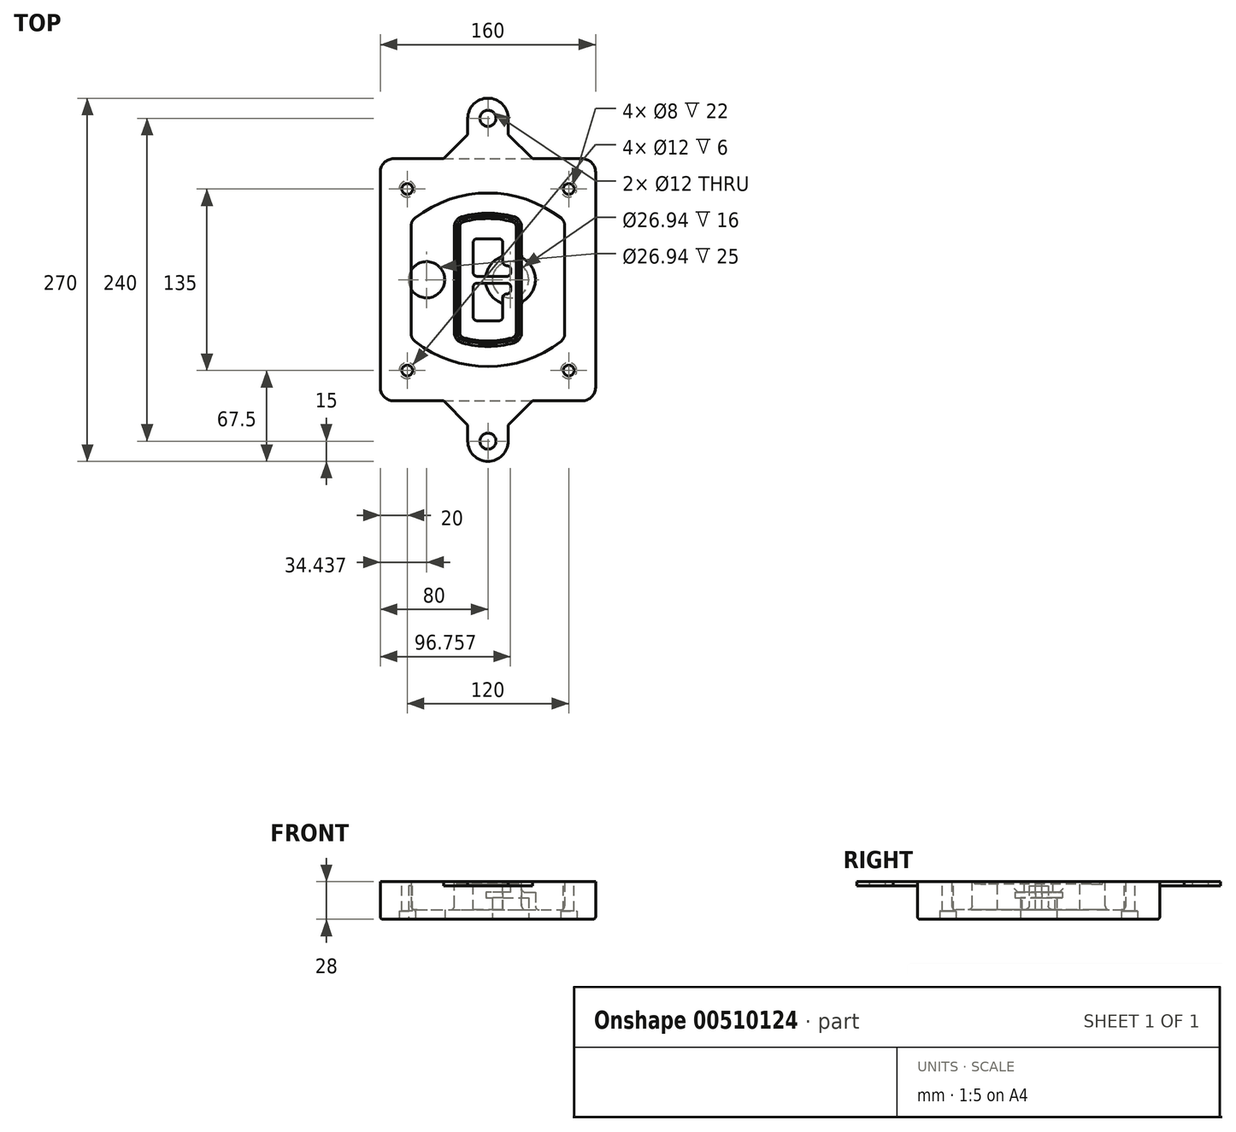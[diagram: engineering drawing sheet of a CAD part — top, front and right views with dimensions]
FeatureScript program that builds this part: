
annotation { "Feature Type Name" : "Feature", "Feature Type Description" : "" }
export const myFeature = defineFeature(function(context is Context, id is Id, definition is map)
    precondition{}
    {
        {
            var Q0;
            Q0=qCreatedBy(makeId("Top.planeOp"),FACE);
            var sketch = newSketch(context, id + "F0", { "sketchPlane" : qUnion([Q0])});
            skPoint(sketch, "E0.rect.middle", {"position": v(0, 0) * mm});
            skLineSegment(sketch, "E1.bottom", {"start": v(-70, -90) * mm, "end": v(70, -90) * mm});
            skLineSegment(sketch, "E1.top", {"start": v(-70, 90) * mm, "end": v(70, 90) * mm});
            skLineSegment(sketch, "E1.left", {"start": v(-80, -80) * mm, "end": v(-80, 80) * mm});
            skLineSegment(sketch, "E1.right", {"start": v(80, -80) * mm, "end": v(80, 80) * mm});
            skLineSegment(sketch, "E2", {"start": v(-80, 90) * mm, "end": v(80, -90) * mm, "construction": true});
            skLineSegment(sketch, "E3", {"start": v(80, 90) * mm, "end": v(-80, -90) * mm, "construction": true});
            skCircle(sketch, "E4", {"center": v(-60, 67.5) * mm, "radius": 4 * mm});
            skCircle(sketch, "E5", {"center": v(60, 67.5) * mm, "radius": 4 * mm});
            skCircle(sketch, "E6", {"center": v(60, -67.5) * mm, "radius": 4 * mm});
            skCircle(sketch, "E7", {"center": v(-60, -67.5) * mm, "radius": 4 * mm});
            skLineSegment(sketch, "E8", {"start": v(-60, 67.5) * mm, "end": v(60, 67.5) * mm, "construction": true});
            skLineSegment(sketch, "E9", {"start": v(60, 67.5) * mm, "end": v(60, -67.5) * mm, "construction": true});
            skLineSegment(sketch, "E10", {"start": v(60, -67.5) * mm, "end": v(-60, -67.5) * mm, "construction": true});
            skLineSegment(sketch, "E11", {"start": v(-60, -67.5) * mm, "end": v(-60, 67.5) * mm, "construction": true});
            skLineSegment(sketch, "E12", {"start": v(-60, 40.3) * mm, "end": v(-60, -40.3) * mm});
            skLineSegment(sketch, "E13", {"start": v(60, 40.3) * mm, "end": v(60, -40.3) * mm});
            skArc(sketch, "E14", {"start": v(56.15, 48.18) * mm, "mid": v(0, 67.5) * mm, "end": v(-56.15, 48.18) * mm});
            skArc(sketch, "E15", {"start": v(-56.15, -48.18) * mm, "mid": v(0, -67.5) * mm, "end": v(56.15, -48.18) * mm});
            skLineSegment(sketch, "E16", {"start": v(-60, 0) * mm, "end": v(60, 0) * mm, "construction": true});
            skPoint(sketch, "E17.visualSharp", {"position": v(-60, -45) * mm});
            skArc(sketch, "E17.filletArc", {"start": v(-60, -40.3) * mm, "mid": v(-58.99, -44.68) * mm, "end": v(-56.15, -48.18) * mm});
            skPoint(sketch, "E18.visualSharp", {"position": v(-60, 45) * mm});
            skArc(sketch, "E18.filletArc", {"start": v(-56.15, 48.18) * mm, "mid": v(-58.99, 44.68) * mm, "end": v(-60, 40.3) * mm});
            skPoint(sketch, "E19.visualSharp", {"position": v(60, 45) * mm});
            skArc(sketch, "E19.filletArc", {"start": v(60, 40.3) * mm, "mid": v(58.99, 44.68) * mm, "end": v(56.15, 48.18) * mm});
            skPoint(sketch, "E20.visualSharp", {"position": v(60, -45) * mm});
            skArc(sketch, "E20.filletArc", {"start": v(56.15, -48.18) * mm, "mid": v(58.99, -44.68) * mm, "end": v(60, -40.3) * mm});
            skPoint(sketch, "E21.visualSharp", {"position": v(-80, 90) * mm});
            skArc(sketch, "E21.filletArc", {"start": v(-70, 90) * mm, "mid": v(-77.07, 87.07) * mm, "end": v(-80, 80) * mm});
            skPoint(sketch, "E22.visualSharp", {"position": v(80, 90) * mm});
            skArc(sketch, "E22.filletArc", {"start": v(80, 80) * mm, "mid": v(77.07, 87.07) * mm, "end": v(70, 90) * mm});
            skPoint(sketch, "E23.visualSharp", {"position": v(80, -90) * mm});
            skArc(sketch, "E23.filletArc", {"start": v(70, -90) * mm, "mid": v(77.07, -87.07) * mm, "end": v(80, -80) * mm});
            skPoint(sketch, "E24.visualSharp", {"position": v(-80, -90) * mm});
            skArc(sketch, "E24.filletArc", {"start": v(-80, -80) * mm, "mid": v(-77.07, -87.07) * mm, "end": v(-70, -90) * mm});
            skArc(sketch, "E25.0", {"start": v(57, 40.3) * mm, "mid": v(56.3, 43.36) * mm, "end": v(54.3, 45.81) * mm});
            skLineSegment(sketch, "E25.1", {"start": v(57, 40.3) * mm, "end": v(57, -40.3) * mm});
            skArc(sketch, "E25.2", {"start": v(54.3, -45.81) * mm, "mid": v(56.3, -43.36) * mm, "end": v(57, -40.3) * mm});
            skArc(sketch, "E25.3", {"start": v(-54.3, -45.81) * mm, "mid": v(0, -64.5) * mm, "end": v(54.3, -45.81) * mm});
            skArc(sketch, "E25.4", {"start": v(-57, -40.3) * mm, "mid": v(-56.3, -43.36) * mm, "end": v(-54.3, -45.81) * mm});
            skArc(sketch, "E25.5", {"start": v(54.3, 45.81) * mm, "mid": v(0, 64.5) * mm, "end": v(-54.3, 45.81) * mm});
            skLineSegment(sketch, "E25.6", {"start": v(-57, 40.3) * mm, "end": v(-57, -40.3) * mm});
            skArc(sketch, "E25.7", {"start": v(-54.3, 45.81) * mm, "mid": v(-56.3, 43.36) * mm, "end": v(-57, 40.3) * mm});
            skArc(sketch, "E26.0", {"start": v(-58.62, 51.33) * mm, "mid": v(-62.58, 46.43) * mm, "end": v(-64, 40.3) * mm});
            skArc(sketch, "E26.1", {"start": v(58.62, 51.33) * mm, "mid": v(0, 71.5) * mm, "end": v(-58.62, 51.33) * mm});
            skArc(sketch, "E26.2", {"start": v(64, 40.3) * mm, "mid": v(62.58, 46.43) * mm, "end": v(58.62, 51.33) * mm});
            skLineSegment(sketch, "E26.3", {"start": v(64, 40.3) * mm, "end": v(64, -40.3) * mm});
            skArc(sketch, "E26.4", {"start": v(58.62, -51.33) * mm, "mid": v(62.58, -46.43) * mm, "end": v(64, -40.3) * mm});
            skLineSegment(sketch, "E26.5", {"start": v(-64, 40.3) * mm, "end": v(-64, -40.3) * mm});
            skArc(sketch, "E26.6", {"start": v(-58.62, -51.33) * mm, "mid": v(0, -71.5) * mm, "end": v(58.62, -51.33) * mm});
            skArc(sketch, "E26.7", {"start": v(-64, -40.3) * mm, "mid": v(-62.58, -46.43) * mm, "end": v(-58.62, -51.33) * mm});
            skSolve(sketch);
        }
        {
            var Q0;
            Q0=makeQuery(id+"F0.imprint","IMPRINT",FACE,{"disambiguationData":[TD([[makeQuery(id+"F0.imprint","IMPRINT",EDGE,{"derivedFrom":sQuery(id+"F0.wireOp",EDGE,"E1.bottom")}),1.0]])]});
            var Q1;
            Q1=makeQuery(id+"F0.imprint","IMPRINT",FACE,{"disambiguationData":[TD([[makeQuery(id+"F0.imprint","IMPRINT",EDGE,{"derivedFrom":sQuery(id+"F0.wireOp",EDGE,"E12")}),1.0]])]});
            var Q2;
            Q2=makeQuery(id+"F0.imprint","IMPRINT",FACE,{"disambiguationData":[TD([[makeQuery(id+"F0.imprint","IMPRINT",EDGE,{"derivedFrom":sQuery(id+"F0.wireOp",EDGE,"E25.0")}),1.0]])]});
            var Q3;
            Q3=makeQuery(id+"F0.imprint","IMPRINT",FACE,{"disambiguationData":[TD([[makeQuery(id+"F0.imprint","IMPRINT",EDGE,{"derivedFrom":sQuery(id+"F0.wireOp",EDGE,"E12")}),-1.0]])]});
            extrude(context, id + "F1", {"entities" : qUnion([Q0, Q1, Q2, Q3]), "oppositeDirection" : true, "depth" : 25 * mm});
        }
        {
            var Q0;
            Q0=makeQuery(id+"F0.imprint","IMPRINT",FACE,{"disambiguationData":[TD([[makeQuery(id+"F0.imprint","IMPRINT",EDGE,{"derivedFrom":sQuery(id+"F0.wireOp",EDGE,"E12")}),1.0]])]});
            extrude(context, id + "F2", {"entities" : qUnion([Q0]), "operationType" : NewBodyOperationType.ADD, "depth" : 3 * mm});
        }
        {
            var Q0;
            Q0=makeQuery(id+"F0.imprint","IMPRINT",FACE,{"disambiguationData":[TD([[makeQuery(id+"F0.imprint","IMPRINT",EDGE,{"derivedFrom":sQuery(id+"F0.wireOp",EDGE,"E25.0")}),1.0]])]});
            extrude(context, id + "F3", {"entities" : qUnion([Q0]), "operationType" : NewBodyOperationType.REMOVE, "oppositeDirection" : true, "depth" : 18 * mm});
        }
        {
            var Q0;
            Q0=makeQuery(id+"F2.opExtrude","CAP_FACE",FACE,{"disambiguationData":[OSD([sQuery(id+"F0.wireOp",EDGE,"E12"),sQuery(id+"F0.wireOp",EDGE,"E13"),sQuery(id+"F0.wireOp",EDGE,"E14"),sQuery(id+"F0.wireOp",EDGE,"E15"),sQuery(id+"F0.wireOp",EDGE,"E17.filletArc"),sQuery(id+"F0.wireOp",EDGE,"E18.filletArc"),sQuery(id+"F0.wireOp",EDGE,"E19.filletArc"),sQuery(id+"F0.wireOp",EDGE,"E20.filletArc"),sQuery(id+"F0.wireOp",EDGE,"E25.0"),sQuery(id+"F0.wireOp",EDGE,"E25.1"),sQuery(id+"F0.wireOp",EDGE,"E25.2"),sQuery(id+"F0.wireOp",EDGE,"E25.3"),sQuery(id+"F0.wireOp",EDGE,"E25.4"),sQuery(id+"F0.wireOp",EDGE,"E25.5"),sQuery(id+"F0.wireOp",EDGE,"E25.6"),sQuery(id+"F0.wireOp",EDGE,"E25.7")])],"isStart":false});
            var sketch = newSketch(context, id + "F4", { "sketchPlane" : qUnion([Q0])});
            skArc(sketch, "E27.0", {"start": v(-19.08, -46.97) * mm, "mid": v(0, -49.5) * mm, "end": v(19.08, -46.97) * mm});
            skArc(sketch, "E28.0", {"start": v(19.08, 46.97) * mm, "mid": v(0, 49.5) * mm, "end": v(-19.08, 46.97) * mm});
            skLineSegment(sketch, "E29", {"start": v(-25, 39.25) * mm, "end": v(-25, -39.25) * mm});
            skLineSegment(sketch, "E30", {"start": v(25, 39.25) * mm, "end": v(25, -39.25) * mm});
            skLineSegment(sketch, "E31", {"start": v(-25, 45.1) * mm, "end": v(25, 45.1) * mm, "construction": true});
            skLineSegment(sketch, "E32", {"start": v(-25, -45.1) * mm, "end": v(25, -45.1) * mm, "construction": true});
            skPoint(sketch, "E33.visualSharp", {"position": v(-25, 45.1) * mm});
            skArc(sketch, "E33.filletArc", {"start": v(-19.08, 46.97) * mm, "mid": v(-23.35, 44.11) * mm, "end": v(-25, 39.25) * mm});
            skPoint(sketch, "E34.visualSharp", {"position": v(25, 45.1) * mm});
            skArc(sketch, "E34.filletArc", {"start": v(25, 39.25) * mm, "mid": v(23.35, 44.11) * mm, "end": v(19.08, 46.97) * mm});
            skPoint(sketch, "E35.visualSharp", {"position": v(25, -45.1) * mm});
            skArc(sketch, "E35.filletArc", {"start": v(19.08, -46.97) * mm, "mid": v(23.35, -44.11) * mm, "end": v(25, -39.25) * mm});
            skPoint(sketch, "E36.visualSharp", {"position": v(-25, -45.1) * mm});
            skArc(sketch, "E36.filletArc", {"start": v(-25, -39.25) * mm, "mid": v(-23.35, -44.11) * mm, "end": v(-19.08, -46.97) * mm});
            skArc(sketch, "E37.0", {"start": v(54.3, 45.81) * mm, "mid": v(0, 64.5) * mm, "end": v(-54.3, 45.81) * mm});
            skArc(sketch, "E37.1", {"start": v(-54.3, 45.81) * mm, "mid": v(-56.3, 43.36) * mm, "end": v(-57, 40.3) * mm});
            skLineSegment(sketch, "E37.2", {"start": v(-57, 40.3) * mm, "end": v(-57, -40.3) * mm});
            skArc(sketch, "E37.3", {"start": v(-57, -40.3) * mm, "mid": v(-56.3, -43.36) * mm, "end": v(-54.3, -45.81) * mm});
            skArc(sketch, "E37.4", {"start": v(-54.3, -45.81) * mm, "mid": v(0, -64.5) * mm, "end": v(54.3, -45.81) * mm});
            skArc(sketch, "E37.5", {"start": v(54.3, -45.81) * mm, "mid": v(56.3, -43.36) * mm, "end": v(57, -40.3) * mm});
            skLineSegment(sketch, "E37.6", {"start": v(57, 40.3) * mm, "end": v(57, -40.3) * mm});
            skArc(sketch, "E37.7", {"start": v(57, 40.3) * mm, "mid": v(56.3, 43.36) * mm, "end": v(54.3, 45.81) * mm});
            skLineSegment(sketch, "E38.0", {"start": v(23, 39.25) * mm, "end": v(23, -39.25) * mm});
            skArc(sketch, "E38.1", {"start": v(18.56, -45.04) * mm, "mid": v(21.76, -42.9) * mm, "end": v(23, -39.25) * mm});
            skArc(sketch, "E38.2", {"start": v(-18.56, -45.04) * mm, "mid": v(0, -47.5) * mm, "end": v(18.56, -45.04) * mm});
            skArc(sketch, "E38.3", {"start": v(-23, -39.25) * mm, "mid": v(-21.76, -42.9) * mm, "end": v(-18.56, -45.04) * mm});
            skLineSegment(sketch, "E38.4", {"start": v(-23, 39.25) * mm, "end": v(-23, -39.25) * mm});
            skArc(sketch, "E38.5", {"start": v(23, 39.25) * mm, "mid": v(21.76, 42.9) * mm, "end": v(18.56, 45.04) * mm});
            skArc(sketch, "E38.6", {"start": v(-18.56, 45.04) * mm, "mid": v(-21.76, 42.9) * mm, "end": v(-23, 39.25) * mm});
            skArc(sketch, "E38.7", {"start": v(18.56, 45.04) * mm, "mid": v(0, 47.5) * mm, "end": v(-18.56, 45.04) * mm});
            skArc(sketch, "E39.0", {"start": v(21, 39.25) * mm, "mid": v(20.18, 41.68) * mm, "end": v(18.04, 43.1) * mm});
            skLineSegment(sketch, "E39.1", {"start": v(21, 39.25) * mm, "end": v(21, -39.25) * mm});
            skArc(sketch, "E39.2", {"start": v(18.04, -43.1) * mm, "mid": v(20.18, -41.68) * mm, "end": v(21, -39.25) * mm});
            skArc(sketch, "E39.3", {"start": v(-18.04, -43.1) * mm, "mid": v(0, -45.5) * mm, "end": v(18.04, -43.1) * mm});
            skArc(sketch, "E39.4", {"start": v(-21, -39.25) * mm, "mid": v(-20.18, -41.68) * mm, "end": v(-18.04, -43.1) * mm});
            skArc(sketch, "E39.5", {"start": v(18.04, 43.1) * mm, "mid": v(0, 45.5) * mm, "end": v(-18.04, 43.1) * mm});
            skLineSegment(sketch, "E39.6", {"start": v(-21, 39.25) * mm, "end": v(-21, -39.25) * mm});
            skArc(sketch, "E39.7", {"start": v(-18.04, 43.1) * mm, "mid": v(-20.18, 41.68) * mm, "end": v(-21, 39.25) * mm});
            skLineSegment(sketch, "E40", {"start": v(-25, 0) * mm, "end": v(25, 0) * mm, "construction": true});
            skLineSegment(sketch, "E41", {"start": v(-11, 5.5) * mm, "end": v(-11, 27.5) * mm});
            skLineSegment(sketch, "E42", {"start": v(-8, 30.5) * mm, "end": v(8, 30.5) * mm});
            skLineSegment(sketch, "E43", {"start": v(11, 27.5) * mm, "end": v(11, 13.5) * mm});
            skLineSegment(sketch, "E44", {"start": v(14, 10.5) * mm, "end": v(14, 10.5) * mm});
            skLineSegment(sketch, "E45", {"start": v(17, 7.5) * mm, "end": v(17, 5.5) * mm});
            skLineSegment(sketch, "E46", {"start": v(14, 2.5) * mm, "end": v(-8, 2.5) * mm});
            skPoint(sketch, "E47.visualSharp", {"position": v(-11, 30.5) * mm});
            skArc(sketch, "E47.filletArc", {"start": v(-8, 30.5) * mm, "mid": v(-10.12, 29.62) * mm, "end": v(-11, 27.5) * mm});
            skPoint(sketch, "E48.visualSharp", {"position": v(11, 30.5) * mm});
            skArc(sketch, "E48.filletArc", {"start": v(11, 27.5) * mm, "mid": v(10.12, 29.62) * mm, "end": v(8, 30.5) * mm});
            skPoint(sketch, "E49.visualSharp", {"position": v(11, 10.5) * mm});
            skArc(sketch, "E49.filletArc", {"start": v(11, 13.5) * mm, "mid": v(11.88, 11.38) * mm, "end": v(14, 10.5) * mm});
            skPoint(sketch, "E50.visualSharp", {"position": v(17, 10.5) * mm});
            skArc(sketch, "E50.filletArc", {"start": v(17, 7.5) * mm, "mid": v(16.12, 9.62) * mm, "end": v(14, 10.5) * mm});
            skPoint(sketch, "E51.visualSharp", {"position": v(17, 2.5) * mm});
            skArc(sketch, "E51.filletArc", {"start": v(14, 2.5) * mm, "mid": v(16.12, 3.38) * mm, "end": v(17, 5.5) * mm});
            skPoint(sketch, "E52.visualSharp", {"position": v(-11, 2.5) * mm});
            skArc(sketch, "E52.filletArc", {"start": v(-11, 5.5) * mm, "mid": v(-10.12, 3.38) * mm, "end": v(-8, 2.5) * mm});
            skLineSegment(sketch, "E53.0.MirrorCS", {"start": v(14, -2.5) * mm, "end": v(-8, -2.5) * mm});
            skArc(sketch, "E54.0.MirrorCS", {"start": v(-11, -5.5) * mm, "mid": v(-10.12, -3.38) * mm, "end": v(-8, -2.5) * mm});
            skLineSegment(sketch, "E55.0.MirrorCS", {"start": v(-11, -5.5) * mm, "end": v(-11, -27.5) * mm});
            skArc(sketch, "E56.0.MirrorCS", {"start": v(-8, -30.5) * mm, "mid": v(-10.12, -29.62) * mm, "end": v(-11, -27.5) * mm});
            skLineSegment(sketch, "E57.0.MirrorCS", {"start": v(-8, -30.5) * mm, "end": v(8, -30.5) * mm});
            skArc(sketch, "E58.0.MirrorCS", {"start": v(11, -27.5) * mm, "mid": v(10.12, -29.62) * mm, "end": v(8, -30.5) * mm});
            skLineSegment(sketch, "E59.0.MirrorCS", {"start": v(11, -27.5) * mm, "end": v(11, -13.5) * mm});
            skArc(sketch, "E60.0.MirrorCS", {"start": v(11, -13.5) * mm, "mid": v(11.88, -11.38) * mm, "end": v(14, -10.5) * mm});
            skArc(sketch, "E61.0.MirrorCS", {"start": v(17, -7.5) * mm, "mid": v(16.12, -9.62) * mm, "end": v(14, -10.5) * mm});
            skLineSegment(sketch, "E62.0.MirrorCS", {"start": v(17, -7.5) * mm, "end": v(17, -5.5) * mm});
            skArc(sketch, "E63.0.MirrorCS", {"start": v(14, -2.5) * mm, "mid": v(16.12, -3.38) * mm, "end": v(17, -5.5) * mm});
            skSolve(sketch);
        }
        {
            var Q0;
            Q0=makeQuery(id+"F4.imprint","IMPRINT",FACE,{"disambiguationData":[TD([[makeQuery(id+"F4.imprint","IMPRINT",EDGE,{"derivedFrom":sQuery(id+"F4.wireOp",EDGE,"E27.0")}),1.0]])]});
            var Q1;
            Q1=makeQuery(id+"F4.imprint","IMPRINT",FACE,{"disambiguationData":[TD([[makeQuery(id+"F4.imprint","IMPRINT",EDGE,{"derivedFrom":sQuery(id+"F4.wireOp",EDGE,"E38.0")}),-1.0]])]});
            var Q2;
            Q2=makeQuery(id+"F4.imprint","IMPRINT",FACE,{"disambiguationData":[TD([[makeQuery(id+"F4.imprint","IMPRINT",EDGE,{"derivedFrom":sQuery(id+"F4.wireOp",EDGE,"E39.0")}),1.0]])]});
            extrude(context, id + "F5", {"entities" : qUnion([Q0, Q1, Q2]), "operationType" : NewBodyOperationType.ADD, "endBound" : BoundingType.UP_TO_NEXT, "oppositeDirection" : true, "depth" : 25 * mm});
        }
        {
            var Q0;
            Q0=makeQuery(id+"F4.imprint","IMPRINT",FACE,{"disambiguationData":[TD([[makeQuery(id+"F4.imprint","IMPRINT",EDGE,{"derivedFrom":sQuery(id+"F4.wireOp",EDGE,"E38.0")}),-1.0]])]});
            extrude(context, id + "F6", {"entities" : qUnion([Q0]), "operationType" : NewBodyOperationType.REMOVE, "oppositeDirection" : true, "depth" : 2 * mm});
        }
        {
            var Q0;
            Q0=makeQuery(id+"F1.opExtrude","CAP_FACE",FACE,{"disambiguationData":[OSD([sQuery(id+"F0.wireOp",EDGE,"E1.bottom"),sQuery(id+"F0.wireOp",EDGE,"E1.top"),sQuery(id+"F0.wireOp",EDGE,"E1.left"),sQuery(id+"F0.wireOp",EDGE,"E1.right"),sQuery(id+"F0.wireOp",EDGE,"E4"),sQuery(id+"F0.wireOp",EDGE,"E5"),sQuery(id+"F0.wireOp",EDGE,"E6"),sQuery(id+"F0.wireOp",EDGE,"E7"),sQuery(id+"F0.wireOp",EDGE,"E21.filletArc"),sQuery(id+"F0.wireOp",EDGE,"E22.filletArc"),sQuery(id+"F0.wireOp",EDGE,"E23.filletArc"),sQuery(id+"F0.wireOp",EDGE,"E24.filletArc")])],"isStart":false});
            var sketch = newSketch(context, id + "F7", { "sketchPlane" : qUnion([Q0])});
            skCircle(sketch, "E64", {"center": v(16.76, 0) * mm, "radius": 13.47 * mm});
            skCircle(sketch, "E65", {"center": v(-45.56, 0) * mm, "radius": 13.47 * mm});
            skLineSegment(sketch, "E66", {"start": v(80, 0) * mm, "end": v(-80, 0) * mm});
            skCircle(sketch, "E67", {"center": v(16.76, 0) * mm, "radius": 18.47 * mm});
            skCircle(sketch, "E68", {"center": v(60, -67.5) * mm, "radius": 6 * mm});
            skCircle(sketch, "E69", {"center": v(-60, -67.5) * mm, "radius": 6 * mm});
            skCircle(sketch, "E70", {"center": v(-60, 67.5) * mm, "radius": 6 * mm});
            skCircle(sketch, "E71", {"center": v(60, 67.5) * mm, "radius": 6 * mm});
            skSolve(sketch);
        }
        {
            var Q0;
            {var subQ1=sQuery(id+"F7.wireOp",EDGE,"E66");var subQ4=sQuery(id+"F7.wireOp",EDGE,"E64");var subQ6=makeQuery(id+"F7.imprint","INTERSECT",VERTEX,{"disambiguationData":[OD(0.0)],"derivedFrom":[subQ4,subQ1]});Q0=makeQuery(id+"F7.imprint","IMPRINT",FACE,{"disambiguationData":[TD([[makeQuery(id+"F7.imprint","IMPRINT",EDGE,{"disambiguationData":[TD([[subQ6,-1.0]])],"derivedFrom":subQ4}),-1.0]])]});}
            var Q1;
            {var subQ0=sQuery(id+"F7.wireOp",EDGE,"E66");var subQ1=sQuery(id+"F7.wireOp",EDGE,"E64");var subQ3=makeQuery(id+"F7.imprint","INTERSECT",VERTEX,{"disambiguationData":[OD(0.0)],"derivedFrom":[subQ1,subQ0]});Q1=makeQuery(id+"F7.imprint","IMPRINT",FACE,{"disambiguationData":[TD([[makeQuery(id+"F7.imprint","IMPRINT",EDGE,{"disambiguationData":[TD([[subQ3,-1.0]])],"derivedFrom":subQ1}),1.0]])]});}
            var Q2;
            {var subQ0=sQuery(id+"F7.wireOp",EDGE,"E66");var subQ1=sQuery(id+"F7.wireOp",EDGE,"E64");var subQ3=makeQuery(id+"F7.imprint","INTERSECT",VERTEX,{"disambiguationData":[OD(0.0)],"derivedFrom":[subQ1,subQ0]});Q2=makeQuery(id+"F7.imprint","IMPRINT",FACE,{"disambiguationData":[TD([[makeQuery(id+"F7.imprint","IMPRINT",EDGE,{"disambiguationData":[TD([[subQ3,1.0]])],"derivedFrom":subQ1}),1.0]])]});}
            var Q3;
            {var subQ1=sQuery(id+"F7.wireOp",EDGE,"E66");var subQ4=sQuery(id+"F7.wireOp",EDGE,"E64");var subQ6=makeQuery(id+"F7.imprint","INTERSECT",VERTEX,{"disambiguationData":[OD(0.0)],"derivedFrom":[subQ4,subQ1]});Q3=makeQuery(id+"F7.imprint","IMPRINT",FACE,{"disambiguationData":[TD([[makeQuery(id+"F7.imprint","IMPRINT",EDGE,{"disambiguationData":[TD([[subQ6,1.0]])],"derivedFrom":subQ4}),-1.0]])]});}
            extrude(context, id + "F8", {"entities" : qUnion([Q0, Q1, Q2, Q3]), "operationType" : NewBodyOperationType.ADD, "oppositeDirection" : true, "depth" : 20 * mm});
        }
        {
            var Q0;
            {var subQ0=sQuery(id+"F7.wireOp",EDGE,"E66");var subQ1=sQuery(id+"F7.wireOp",EDGE,"E64");var subQ3=makeQuery(id+"F7.imprint","INTERSECT",VERTEX,{"disambiguationData":[OD(0.0)],"derivedFrom":[subQ1,subQ0]});Q0=makeQuery(id+"F7.imprint","IMPRINT",FACE,{"disambiguationData":[TD([[makeQuery(id+"F7.imprint","IMPRINT",EDGE,{"disambiguationData":[TD([[subQ3,-1.0]])],"derivedFrom":subQ1}),1.0]])]});}
            var Q1;
            {var subQ0=sQuery(id+"F7.wireOp",EDGE,"E66");var subQ1=sQuery(id+"F7.wireOp",EDGE,"E64");var subQ3=makeQuery(id+"F7.imprint","INTERSECT",VERTEX,{"disambiguationData":[OD(0.0)],"derivedFrom":[subQ1,subQ0]});Q1=makeQuery(id+"F7.imprint","IMPRINT",FACE,{"disambiguationData":[TD([[makeQuery(id+"F7.imprint","IMPRINT",EDGE,{"disambiguationData":[TD([[subQ3,1.0]])],"derivedFrom":subQ1}),1.0]])]});}
            extrude(context, id + "F9", {"entities" : qUnion([Q0, Q1]), "operationType" : NewBodyOperationType.REMOVE, "oppositeDirection" : true, "depth" : 16 * mm});
        }
        {
            var Q0;
            {var subQ0=sQuery(id+"F7.wireOp",EDGE,"E66");var subQ1=sQuery(id+"F7.wireOp",EDGE,"E65");var subQ3=makeQuery(id+"F7.imprint","INTERSECT",VERTEX,{"disambiguationData":[OD(0.0)],"derivedFrom":[subQ1,subQ0]});Q0=makeQuery(id+"F7.imprint","IMPRINT",FACE,{"disambiguationData":[TD([[makeQuery(id+"F7.imprint","IMPRINT",EDGE,{"disambiguationData":[TD([[subQ3,-1.0]])],"derivedFrom":subQ1}),1.0]])]});}
            var Q1;
            {var subQ0=sQuery(id+"F7.wireOp",EDGE,"E66");var subQ1=sQuery(id+"F7.wireOp",EDGE,"E65");var subQ3=makeQuery(id+"F7.imprint","INTERSECT",VERTEX,{"disambiguationData":[OD(0.0)],"derivedFrom":[subQ1,subQ0]});Q1=makeQuery(id+"F7.imprint","IMPRINT",FACE,{"disambiguationData":[TD([[makeQuery(id+"F7.imprint","IMPRINT",EDGE,{"disambiguationData":[TD([[subQ3,1.0]])],"derivedFrom":subQ1}),1.0]])]});}
            extrude(context, id + "F10", {"entities" : qUnion([Q0, Q1]), "operationType" : NewBodyOperationType.REMOVE, "oppositeDirection" : true, "depth" : 25 * mm});
        }
        {
            var Q0;
            Q0=makeQuery(id+"F7.imprint","IMPRINT",FACE,{"disambiguationData":[TD([[makeQuery(id+"F7.imprint","IMPRINT",EDGE,{"derivedFrom":sQuery(id+"F7.wireOp",EDGE,"E68")}),1.0]])]});
            var Q1;
            Q1=makeQuery(id+"F7.imprint","IMPRINT",FACE,{"disambiguationData":[TD([[makeQuery(id+"F7.imprint","IMPRINT",EDGE,{"derivedFrom":makeQuery(id+"F1.opExtrude","CAP_EDGE",EDGE,{"disambiguationData":[OSD([sQuery(id+"F0.wireOp",EDGE,"E5")])],"isStart":false})}),-1.0]])]});
            var Q2;
            Q2=makeQuery(id+"F7.imprint","IMPRINT",FACE,{"disambiguationData":[TD([[makeQuery(id+"F7.imprint","IMPRINT",EDGE,{"derivedFrom":sQuery(id+"F7.wireOp",EDGE,"E69")}),1.0]])]});
            var Q3;
            Q3=makeQuery(id+"F7.imprint","IMPRINT",FACE,{"disambiguationData":[TD([[makeQuery(id+"F7.imprint","IMPRINT",EDGE,{"derivedFrom":makeQuery(id+"F1.opExtrude","CAP_EDGE",EDGE,{"disambiguationData":[OSD([sQuery(id+"F0.wireOp",EDGE,"E4")])],"isStart":false})}),-1.0]])]});
            var Q4;
            Q4=makeQuery(id+"F7.imprint","IMPRINT",FACE,{"disambiguationData":[TD([[makeQuery(id+"F7.imprint","IMPRINT",EDGE,{"derivedFrom":sQuery(id+"F7.wireOp",EDGE,"E70")}),1.0]])]});
            var Q5;
            Q5=makeQuery(id+"F7.imprint","IMPRINT",FACE,{"disambiguationData":[TD([[makeQuery(id+"F7.imprint","IMPRINT",EDGE,{"derivedFrom":makeQuery(id+"F1.opExtrude","CAP_EDGE",EDGE,{"disambiguationData":[OSD([sQuery(id+"F0.wireOp",EDGE,"E7")])],"isStart":false})}),-1.0]])]});
            var Q6;
            Q6=makeQuery(id+"F7.imprint","IMPRINT",FACE,{"disambiguationData":[TD([[makeQuery(id+"F7.imprint","IMPRINT",EDGE,{"derivedFrom":sQuery(id+"F7.wireOp",EDGE,"E71")}),1.0]])]});
            var Q7;
            Q7=makeQuery(id+"F7.imprint","IMPRINT",FACE,{"disambiguationData":[TD([[makeQuery(id+"F7.imprint","IMPRINT",EDGE,{"derivedFrom":makeQuery(id+"F1.opExtrude","CAP_EDGE",EDGE,{"disambiguationData":[OSD([sQuery(id+"F0.wireOp",EDGE,"E6")])],"isStart":false})}),-1.0]])]});
            extrude(context, id + "F11", {"entities" : qUnion([Q0, Q1, Q2, Q3, Q4, Q5, Q6, Q7]), "operationType" : NewBodyOperationType.REMOVE, "oppositeDirection" : true, "depth" : 6 * mm});
        }
        {
            var Q0;
            Q0=makeQuery(id+"F9.boolean.opBoolean","COPY",FACE,{"derivedFrom":makeQuery(id+"F9.opExtrude","CAP_FACE",FACE,{"disambiguationData":[OSD([sQuery(id+"F7.wireOp",EDGE,"E64")])],"isStart":false})});
            var sketch = newSketch(context, id + "F12", { "sketchPlane" : qUnion([Q0])});
            skArc(sketch, "E72.0", {"start": v(11, 17.55) * mm, "mid": v(2.57, 11.82) * mm, "end": v(-1.54, 2.5) * mm});
            skArc(sketch, "E72.1", {"start": v(-1.54, -2.5) * mm, "mid": v(2.57, -11.82) * mm, "end": v(11, -17.55) * mm});
            skLineSegment(sketch, "E73", {"start": v(-1.54, -2.5) * mm, "end": v(14, -2.5) * mm});
            skLineSegment(sketch, "E74.0", {"start": v(14, 2.5) * mm, "end": v(-1.54, 2.5) * mm});
            skArc(sketch, "E74.1", {"start": v(14, 2.5) * mm, "mid": v(16.12, 3.38) * mm, "end": v(17, 5.5) * mm});
            skLineSegment(sketch, "E74.2", {"start": v(17, 7.5) * mm, "end": v(17, 5.5) * mm});
            skArc(sketch, "E74.3", {"start": v(17, 7.5) * mm, "mid": v(16.12, 9.62) * mm, "end": v(14, 10.5) * mm});
            skArc(sketch, "E74.4", {"start": v(11, 13.5) * mm, "mid": v(11.88, 11.38) * mm, "end": v(14, 10.5) * mm});
            skLineSegment(sketch, "E74.5", {"start": v(11, 17.55) * mm, "end": v(11, 13.5) * mm});
            skLineSegment(sketch, "E74.7", {"start": v(14, -2.5) * mm, "end": v(-1.54, -2.5) * mm});
            skArc(sketch, "E74.8", {"start": v(14, -2.5) * mm, "mid": v(16.12, -3.38) * mm, "end": v(17, -5.5) * mm});
            skLineSegment(sketch, "E74.9", {"start": v(17, -7.5) * mm, "end": v(17, -5.5) * mm});
            skArc(sketch, "E74.10", {"start": v(17, -7.5) * mm, "mid": v(16.12, -9.62) * mm, "end": v(14, -10.5) * mm});
            skArc(sketch, "E74.11", {"start": v(11, -13.5) * mm, "mid": v(11.88, -11.38) * mm, "end": v(14, -10.5) * mm});
            skLineSegment(sketch, "E74.12", {"start": v(11, -17.55) * mm, "end": v(11, -13.5) * mm});
            skPoint(sketch, "E75.orphan", {"position": v(11, -27.5) * mm});
            skPoint(sketch, "E76.orphan", {"position": v(-8, -2.5) * mm});
            skPoint(sketch, "E77.orphan", {"position": v(-8, 2.5) * mm});
            skPoint(sketch, "E78.orphan", {"position": v(11, 27.5) * mm});
            skSolve(sketch);
        }
        {
            var Q0;
            {var subQ7=sQuery(id+"F12.wireOp",EDGE,"E72.0");var subQ14=sQuery(id+"F12.wireOp",EDGE,"E72.1");var subQ16=sQuery(id+"F12.wireOp",EDGE,"E74.1");var subQ18=sQuery(id+"F12.wireOp",EDGE,"E74.8");Q0=qUnion([makeQuery(id+"F12.imprint","IMPRINT",FACE,{"disambiguationData":[TD([[makeQuery(id+"F12.imprint","IMPRINT",EDGE,{"derivedFrom":subQ7}),1.0]])]}),makeQuery(id+"F12.imprint","IMPRINT",FACE,{"disambiguationData":[TD([[makeQuery(id+"F12.imprint","IMPRINT",EDGE,{"derivedFrom":subQ14}),1.0]])]}),makeQuery(id+"F12.imprint","IMPRINT",FACE,{"disambiguationData":[TD([[makeQuery(id+"F12.imprint","IMPRINT",EDGE,{"derivedFrom":subQ16}),1.0]])]}),makeQuery(id+"F12.imprint","IMPRINT",FACE,{"disambiguationData":[TD([[makeQuery(id+"F12.imprint","IMPRINT",EDGE,{"derivedFrom":subQ18}),-1.0]])]})]);}
            var Q1;
            Q1=makeQuery(id+"F5.boolean.opBoolean","SPLIT",FACE,{"disambiguationData":[TD([makeQuery(id+"F5.opExtrude","SWEPT_FACE",FACE,{"disambiguationData":[OSD([sQuery(id+"F4.wireOp",EDGE,"E41")])]})])],"derivedFrom":makeQuery(id+"F3.boolean.opBoolean","COPY",FACE,{"derivedFrom":makeQuery(id+"F3.opExtrude","CAP_FACE",FACE,{"disambiguationData":[OSD([sQuery(id+"F0.wireOp",EDGE,"E25.0"),sQuery(id+"F0.wireOp",EDGE,"E25.1"),sQuery(id+"F0.wireOp",EDGE,"E25.2"),sQuery(id+"F0.wireOp",EDGE,"E25.3"),sQuery(id+"F0.wireOp",EDGE,"E25.4"),sQuery(id+"F0.wireOp",EDGE,"E25.5"),sQuery(id+"F0.wireOp",EDGE,"E25.6"),sQuery(id+"F0.wireOp",EDGE,"E25.7")])],"isStart":false})})});
            extrude(context, id + "F13", {"entities" : qUnion([Q0]), "operationType" : NewBodyOperationType.REMOVE, "endBound" : BoundingType.UP_TO_SURFACE, "endBoundEntityFace" : qUnion([Q1]), "depth" : 25 * mm});
        }
        {
            var Q0;
            Q0=makeQuery(id+"F3.boolean.opBoolean","COPY",EDGE,{"derivedFrom":makeQuery(id+"F3.opExtrude","CAP_EDGE",EDGE,{"disambiguationData":[OSD([sQuery(id+"F0.wireOp",EDGE,"E25.6")])],"isStart":false})});
            var Q1;
            Q1=makeQuery(id+"F8.boolean.opBoolean","INTERSECT",EDGE,{"derivedFrom":[makeQuery(id+"F5.opExtrude","SWEPT_FACE",FACE,{"disambiguationData":[OSD([sQuery(id+"F4.wireOp",EDGE,"E30")])]}),makeQuery(id+"F8.opExtrude","CAP_FACE",FACE,{"disambiguationData":[OSD([sQuery(id+"F7.wireOp",EDGE,"E67")])],"isStart":false})]});
            var Q2;
            Q2=makeQuery(id+"F8.boolean.opBoolean","INTERSECT",EDGE,{"disambiguationData":[OD(1.0)],"derivedFrom":[makeQuery(id+"F5.opExtrude","SWEPT_FACE",FACE,{"disambiguationData":[OSD([sQuery(id+"F4.wireOp",EDGE,"E30")])]}),makeQuery(id+"F8.opExtrude","SWEPT_FACE",FACE,{"disambiguationData":[OSD([sQuery(id+"F7.wireOp",EDGE,"E67")])]})]});
            var Q3;
            {var subQ0=sQuery(id+"F4.wireOp",EDGE,"E30");Q3=makeQuery(id+"F8.boolean.opBoolean","SPLIT",EDGE,{"disambiguationData":[TD([makeQuery(id+"F5.opExtrude","SWEPT_FACE",FACE,{"disambiguationData":[OSD([sQuery(id+"F4.wireOp",EDGE,"E35.filletArc")])]})])],"derivedFrom":makeQuery(id+"F5.opExtrude","CAP_EDGE",EDGE,{"disambiguationData":[OSD([subQ0])],"isStart":false})});}
            var Q4;
            {var subQ0=sQuery(id+"F0.wireOp",EDGE,"E25.7");var subQ1=sQuery(id+"F0.wireOp",EDGE,"E25.1");var subQ2=sQuery(id+"F0.wireOp",EDGE,"E25.6");var subQ3=sQuery(id+"F0.wireOp",EDGE,"E25.5");var subQ4=sQuery(id+"F0.wireOp",EDGE,"E25.4");var subQ5=sQuery(id+"F0.wireOp",EDGE,"E25.0");var subQ6=sQuery(id+"F0.wireOp",EDGE,"E25.2");var subQ7=sQuery(id+"F0.wireOp",EDGE,"E25.3");Q4=makeQuery(id+"F8.boolean.opBoolean","INTERSECT",EDGE,{"derivedFrom":[makeQuery(id+"F5.boolean.opBoolean","SPLIT",FACE,{"disambiguationData":[TD([makeQuery(id+"F2.opExtrude","SWEPT_FACE",FACE,{"disambiguationData":[OSD([subQ5])]})])],"derivedFrom":makeQuery(id+"F3.boolean.opBoolean","COPY",FACE,{"derivedFrom":makeQuery(id+"F3.opExtrude","CAP_FACE",FACE,{"disambiguationData":[OSD([subQ5,subQ1,subQ6,subQ7,subQ4,subQ3,subQ2,subQ0])],"isStart":false})})}),makeQuery(id+"F8.opExtrude","SWEPT_FACE",FACE,{"disambiguationData":[OSD([sQuery(id+"F7.wireOp",EDGE,"E67")])]})]});}
            var Q5;
            Q5=makeQuery(id+"F8.boolean.opBoolean","INTERSECT",EDGE,{"disambiguationData":[OD(0.0)],"derivedFrom":[makeQuery(id+"F5.opExtrude","SWEPT_FACE",FACE,{"disambiguationData":[OSD([sQuery(id+"F4.wireOp",EDGE,"E30")])]}),makeQuery(id+"F8.opExtrude","SWEPT_FACE",FACE,{"disambiguationData":[OSD([sQuery(id+"F7.wireOp",EDGE,"E67")])]})]});
            fillet(context, id + "F14", {"entities" : qUnion([Q0, Q1, Q2, Q3, Q4, Q5]), "radius" : 3 * mm, "tangentPropagation" : true, "allowEdgeOverflow" : false});
        }
        {
            var Q0;
            Q0=makeQuery(id+"F1.opExtrude","CAP_EDGE",EDGE,{"disambiguationData":[OSD([sQuery(id+"F0.wireOp",EDGE,"E1.bottom")])],"isStart":false});
            fillet(context, id + "F15", {"entities" : qUnion([Q0]), "radius" : 2 * mm, "tangentPropagation" : true, "allowEdgeOverflow" : false});
        }
        {
            var Q0;
            {var subQ0=sQuery(id+"F0.wireOp",EDGE,"E21.filletArc");var subQ1=sQuery(id+"F0.wireOp",EDGE,"E7");var subQ2=sQuery(id+"F0.wireOp",EDGE,"E6");var subQ3=sQuery(id+"F0.wireOp",EDGE,"E5");var subQ4=sQuery(id+"F0.wireOp",EDGE,"E4");var subQ5=sQuery(id+"F0.wireOp",EDGE,"E22.filletArc");var subQ6=sQuery(id+"F0.wireOp",EDGE,"E1.bottom");var subQ7=sQuery(id+"F0.wireOp",EDGE,"E1.right");var subQ8=sQuery(id+"F0.wireOp",EDGE,"E1.top");var subQ9=sQuery(id+"F0.wireOp",EDGE,"E1.left");var subQ10=sQuery(id+"F0.wireOp",EDGE,"E23.filletArc");var subQ11=sQuery(id+"F0.wireOp",EDGE,"E24.filletArc");Q0=makeQuery(id+"F2.boolean.opBoolean","SPLIT",FACE,{"disambiguationData":[TD([makeQuery(id+"F1.opExtrude","SWEPT_FACE",FACE,{"disambiguationData":[OSD([subQ6])]})])],"derivedFrom":makeQuery(id+"F1.opExtrude","CAP_FACE",FACE,{"disambiguationData":[OSD([subQ6,subQ8,subQ9,subQ7,subQ4,subQ3,subQ2,subQ1,subQ0,subQ5,subQ10,subQ11])],"isStart":true})});}
            var sketch = newSketch(context, id + "F16", { "sketchPlane" : qUnion([Q0])});
            skCircle(sketch, "E79.0", {"center": v(60, 67.5) * mm, "radius": 4 * mm});
            skCircle(sketch, "E79.1", {"center": v(-60, 67.5) * mm, "radius": 4 * mm});
            skCircle(sketch, "E79.2", {"center": v(-60, -67.5) * mm, "radius": 4 * mm});
            skCircle(sketch, "E79.3", {"center": v(60, -67.5) * mm, "radius": 4 * mm});
            skLineSegment(sketch, "E79.4", {"start": v(-70, -90) * mm, "end": v(70, -90) * mm});
            skArc(sketch, "E79.5", {"start": v(70, -90) * mm, "mid": v(77.07, -87.07) * mm, "end": v(80, -80) * mm});
            skLineSegment(sketch, "E79.6", {"start": v(80, -80) * mm, "end": v(80, 80) * mm});
            skLineSegment(sketch, "E79.7", {"start": v(-70, 90) * mm, "end": v(70, 90) * mm});
            skArc(sketch, "E79.8", {"start": v(80, 80) * mm, "mid": v(77.07, 87.07) * mm, "end": v(70, 90) * mm});
            skArc(sketch, "E79.9", {"start": v(-70, 90) * mm, "mid": v(-77.07, 87.07) * mm, "end": v(-80, 80) * mm});
            skLineSegment(sketch, "E79.10", {"start": v(-80, -80) * mm, "end": v(-80, 80) * mm});
            skArc(sketch, "E79.11", {"start": v(-80, -80) * mm, "mid": v(-77.07, -87.07) * mm, "end": v(-70, -90) * mm});
            skArc(sketch, "E79.12", {"start": v(-56.15, -48.18) * mm, "mid": v(0, -67.5) * mm, "end": v(56.15, -48.18) * mm});
            skLineSegment(sketch, "E79.13", {"start": v(-60, 40.3) * mm, "end": v(-60, -40.3) * mm});
            skArc(sketch, "E79.14", {"start": v(56.15, 48.18) * mm, "mid": v(0, 67.5) * mm, "end": v(-56.15, 48.18) * mm});
            skLineSegment(sketch, "E79.15", {"start": v(60, 40.3) * mm, "end": v(60, -40.3) * mm});
            skArc(sketch, "E79.16", {"start": v(60, 40.3) * mm, "mid": v(58.99, 44.68) * mm, "end": v(56.15, 48.18) * mm});
            skArc(sketch, "E79.17", {"start": v(-56.15, 48.18) * mm, "mid": v(-58.99, 44.68) * mm, "end": v(-60, 40.3) * mm});
            skArc(sketch, "E79.18", {"start": v(-60, -40.3) * mm, "mid": v(-58.99, -44.68) * mm, "end": v(-56.15, -48.18) * mm});
            skArc(sketch, "E79.19", {"start": v(56.15, -48.18) * mm, "mid": v(58.99, -44.68) * mm, "end": v(60, -40.3) * mm});
            skLineSegment(sketch, "E80", {"start": v(0, 90) * mm, "end": v(0, 120) * mm, "construction": true});
            skCircle(sketch, "E81", {"center": v(0, 120) * mm, "radius": 6 * mm});
            skArc(sketch, "E82", {"start": v(-15, 120) * mm, "mid": v(0, 135) * mm, "end": v(15, 120) * mm});
            skLineSegment(sketch, "E83", {"start": v(-15, 120) * mm, "end": v(-15, 108) * mm});
            skLineSegment(sketch, "E84", {"start": v(15, 120) * mm, "end": v(15, 108) * mm});
            skLineSegment(sketch, "E85", {"start": v(-15, 108) * mm, "end": v(-33, 90) * mm});
            skLineSegment(sketch, "E86", {"start": v(15, 108) * mm, "end": v(33, 90) * mm});
            skLineSegment(sketch, "E87", {"start": v(-80, 0) * mm, "end": v(80, 0) * mm, "construction": true});
            skArc(sketch, "E88.MirrorCS", {"start": v(-56.15, -48.18) * mm, "mid": v(-58.99, -44.68) * mm, "end": v(-60, -40.3) * mm});
            skArc(sketch, "E89.MirrorCS", {"start": v(60, -40.3) * mm, "mid": v(58.99, -44.68) * mm, "end": v(56.15, -48.18) * mm});
            skLineSegment(sketch, "E90.MirrorCS", {"start": v(0, -90) * mm, "end": v(0, -120) * mm, "construction": true});
            skArc(sketch, "E91.MirrorCS", {"start": v(56.15, -48.18) * mm, "mid": v(0, -67.5) * mm, "end": v(-56.15, -48.18) * mm});
            skLineSegment(sketch, "E92.MirrorCS", {"start": v(15, -108) * mm, "end": v(33, -90) * mm});
            skLineSegment(sketch, "E93.MirrorCS", {"start": v(-15, -108) * mm, "end": v(-33, -90) * mm});
            skCircle(sketch, "E94.MirrorC", {"center": v(0, -120) * mm, "radius": 6 * mm});
            skLineSegment(sketch, "E95.MirrorCS", {"start": v(-15, -120) * mm, "end": v(-15, -108) * mm});
            skLineSegment(sketch, "E96.MirrorCS", {"start": v(15, -120) * mm, "end": v(15, -108) * mm});
            skArc(sketch, "E97.MirrorCS", {"start": v(-15, -120) * mm, "mid": v(0, -135) * mm, "end": v(15, -120) * mm});
            skArc(sketch, "E98.MirrorCS", {"start": v(-70, -90) * mm, "mid": v(-77.07, -87.07) * mm, "end": v(-80, -80) * mm});
            skArc(sketch, "E99.MirrorCS", {"start": v(80, -80) * mm, "mid": v(77.07, -87.07) * mm, "end": v(70, -90) * mm});
            skSolve(sketch);
        }
        {
            var Q0;
            Q0=makeQuery(id+"F16.imprint","IMPRINT",FACE,{"disambiguationData":[TD([[makeQuery(id+"F16.imprint","IMPRINT",EDGE,{"derivedFrom":sQuery(id+"F16.wireOp",EDGE,"E79.0")}),-1.0]])]});
            var Q1;
            {var subQ1=sQuery(id+"F16.wireOp",EDGE,"E92.MirrorCS");Q1=makeQuery(id+"F16.imprint","IMPRINT",FACE,{"disambiguationData":[TD([[makeQuery(id+"F16.imprint","IMPRINT",EDGE,{"derivedFrom":subQ1}),1.0]])]});}
            var Q2;
            Q2=makeQuery(id+"F16.imprint","IMPRINT",FACE,{"disambiguationData":[TD([[makeQuery(id+"F16.imprint","IMPRINT",EDGE,{"derivedFrom":sQuery(id+"F16.wireOp",EDGE,"E81")}),-1.0]])]});
            var Q3;
            Q3=makeQuery(id+"F2.opExtrude","CAP_FACE",FACE,{"disambiguationData":[OSD([sQuery(id+"F0.wireOp",EDGE,"E12"),sQuery(id+"F0.wireOp",EDGE,"E13"),sQuery(id+"F0.wireOp",EDGE,"E14"),sQuery(id+"F0.wireOp",EDGE,"E15"),sQuery(id+"F0.wireOp",EDGE,"E17.filletArc"),sQuery(id+"F0.wireOp",EDGE,"E18.filletArc"),sQuery(id+"F0.wireOp",EDGE,"E19.filletArc"),sQuery(id+"F0.wireOp",EDGE,"E20.filletArc"),sQuery(id+"F0.wireOp",EDGE,"E25.0"),sQuery(id+"F0.wireOp",EDGE,"E25.1"),sQuery(id+"F0.wireOp",EDGE,"E25.2"),sQuery(id+"F0.wireOp",EDGE,"E25.3"),sQuery(id+"F0.wireOp",EDGE,"E25.4"),sQuery(id+"F0.wireOp",EDGE,"E25.5"),sQuery(id+"F0.wireOp",EDGE,"E25.6"),sQuery(id+"F0.wireOp",EDGE,"E25.7")])],"isStart":false});
            extrude(context, id + "F17", {"entities" : qUnion([Q0, Q1, Q2]), "operationType" : NewBodyOperationType.ADD, "endBound" : BoundingType.UP_TO_SURFACE, "endBoundEntityFace" : qUnion([Q3]), "depth" : 3 * mm});
        }
    });
